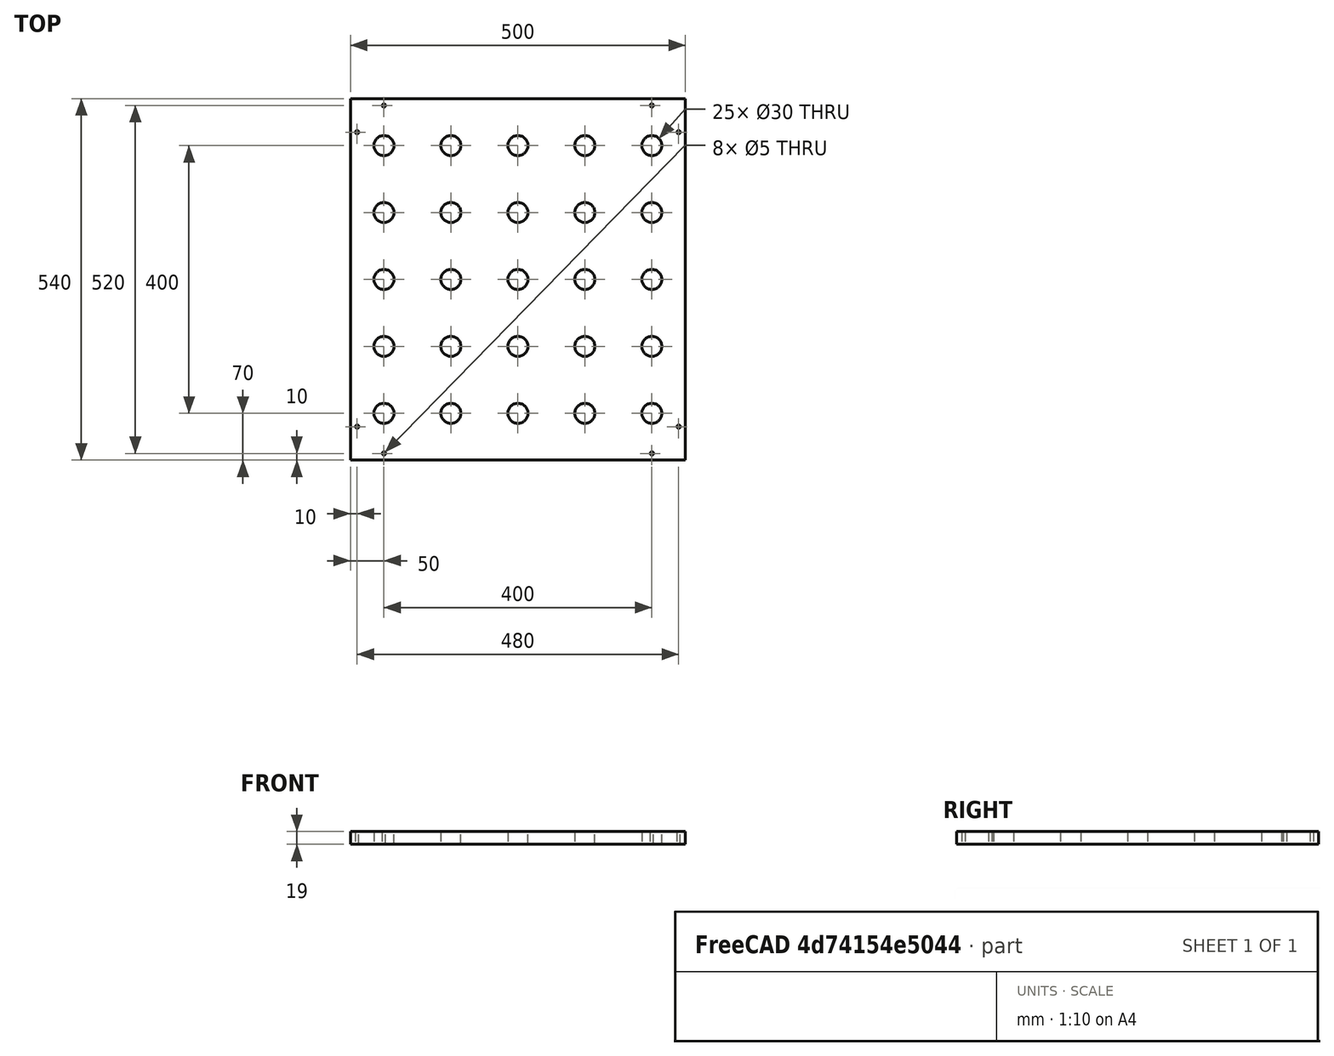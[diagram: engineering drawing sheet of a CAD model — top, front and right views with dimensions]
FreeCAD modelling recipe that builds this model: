
FCSTD DOCUMENT  (FreeCAD 0.19R)
Label: plate
License: All rights reserved
LicenseURL: http://en.wikipedia.org/wiki/All_rights_reserved
objects: TechDraw::DrawViewDimension×12, TechDraw::DrawViewPart×2, Sketcher::SketchObject×1, PartDesign::Body×1, Part::Extrusion×1, TechDraw::DrawSVGTemplate×1, TechDraw::DrawViewAnnotation×1, TechDraw::DrawPage×1
note: 3 computed .brp shape members not serialized (recipe doc carries the construction recipe); baked Part::Feature solids carry a one-line shape summary decoded from their .brp

FEATURE [Sketcher::SketchObject] Sketch
  FullyConstrained = true
  MapMode = 5
  Support = -> [XY_Plane]
  sketch-geometry (37):
    g0: LineSegment StartX=-500 StartY=540 StartZ=0 EndX=0 EndY=540 EndZ=0
    g1: LineSegment StartX=0 StartY=540 StartZ=0 EndX=0 EndY=0 EndZ=0
    g2: LineSegment StartX=0 StartY=0 StartZ=0 EndX=-500 EndY=0 EndZ=0
    g3: LineSegment StartX=-500 StartY=0 StartZ=0 EndX=-500 EndY=540 EndZ=0
    g4: Circle CenterX=-450 CenterY=470 CenterZ=0 NormalX=0 NormalY=0 NormalZ=1 AngleXU=0 Radius=15
    g5: Circle CenterX=-350 CenterY=470 CenterZ=0 NormalX=0 NormalY=0 NormalZ=1 AngleXU=0 Radius=15
    g6: Circle CenterX=-250 CenterY=470 CenterZ=0 NormalX=0 NormalY=0 NormalZ=1 AngleXU=0 Radius=15
    g7: Circle CenterX=-150 CenterY=470 CenterZ=0 NormalX=0 NormalY=0 NormalZ=1 AngleXU=0 Radius=15
    g8: Circle CenterX=-50 CenterY=470 CenterZ=0 NormalX=0 NormalY=0 NormalZ=1 AngleXU=0 Radius=15
    g9: Circle CenterX=-450 CenterY=370 CenterZ=0 NormalX=0 NormalY=0 NormalZ=1 AngleXU=0 Radius=15
    g10: Circle CenterX=-450 CenterY=270 CenterZ=0 NormalX=0 NormalY=0 NormalZ=1 AngleXU=0 Radius=15
    g11: Circle CenterX=-450 CenterY=170 CenterZ=0 NormalX=0 NormalY=0 NormalZ=1 AngleXU=0 Radius=15
    g12: Circle CenterX=-450 CenterY=70 CenterZ=0 NormalX=0 NormalY=0 NormalZ=1 AngleXU=0 Radius=15
    g13: Circle CenterX=-350 CenterY=370 CenterZ=0 NormalX=0 NormalY=0 NormalZ=1 AngleXU=0 Radius=15
    g14: Circle CenterX=-250 CenterY=370 CenterZ=0 NormalX=0 NormalY=0 NormalZ=1 AngleXU=0 Radius=15
    g15: Circle CenterX=-150 CenterY=370 CenterZ=0 NormalX=0 NormalY=0 NormalZ=1 AngleXU=0 Radius=15
    g16: Circle CenterX=-50 CenterY=370 CenterZ=0 NormalX=0 NormalY=0 NormalZ=1 AngleXU=0 Radius=15
    g17: Circle CenterX=-350 CenterY=270 CenterZ=0 NormalX=0 NormalY=0 NormalZ=1 AngleXU=0 Radius=15
    g18: Circle CenterX=-250 CenterY=270 CenterZ=0 NormalX=0 NormalY=0 NormalZ=1 AngleXU=0 Radius=15
    g19: Circle CenterX=-150 CenterY=270 CenterZ=0 NormalX=0 NormalY=0 NormalZ=1 AngleXU=0 Radius=15
    g20: Circle CenterX=-50 CenterY=270 CenterZ=0 NormalX=0 NormalY=0 NormalZ=1 AngleXU=0 Radius=15
    g21: Circle CenterX=-350 CenterY=170 CenterZ=0 NormalX=0 NormalY=0 NormalZ=1 AngleXU=0 Radius=15
    g22: Circle CenterX=-250 CenterY=170 CenterZ=0 NormalX=0 NormalY=0 NormalZ=1 AngleXU=0 Radius=15
    g23: Circle CenterX=-150 CenterY=170 CenterZ=0 NormalX=0 NormalY=0 NormalZ=1 AngleXU=0 Radius=15
    g24: Circle CenterX=-50 CenterY=170 CenterZ=0 NormalX=0 NormalY=0 NormalZ=1 AngleXU=0 Radius=15
    g25: Circle CenterX=-350 CenterY=70 CenterZ=0 NormalX=0 NormalY=0 NormalZ=1 AngleXU=0 Radius=15
    g26: Circle CenterX=-250 CenterY=70 CenterZ=0 NormalX=0 NormalY=0 NormalZ=1 AngleXU=0 Radius=15
    g27: Circle CenterX=-150 CenterY=70 CenterZ=0 NormalX=0 NormalY=0 NormalZ=1 AngleXU=0 Radius=15
    g28: Circle CenterX=-50 CenterY=70 CenterZ=0 NormalX=0 NormalY=0 NormalZ=1 AngleXU=0 Radius=15
    g29: Circle CenterX=-450 CenterY=530 CenterZ=0 NormalX=0 NormalY=0 NormalZ=1 AngleXU=0 Radius=2.5
    g30: Circle CenterX=-490 CenterY=490 CenterZ=0 NormalX=0 NormalY=0 NormalZ=1 AngleXU=0 Radius=2.5
    g31: Circle CenterX=-50 CenterY=530 CenterZ=0 NormalX=0 NormalY=0 NormalZ=1 AngleXU=0 Radius=2.5
    g32: Circle CenterX=-10 CenterY=490 CenterZ=0 NormalX=0 NormalY=0 NormalZ=1 AngleXU=0 Radius=2.5
    g33: Circle CenterX=-490 CenterY=50 CenterZ=0 NormalX=0 NormalY=0 NormalZ=1 AngleXU=0 Radius=2.5
    g34: Circle CenterX=-450 CenterY=10 CenterZ=0 NormalX=0 NormalY=0 NormalZ=1 AngleXU=0 Radius=2.5
    g35: Circle CenterX=-10 CenterY=50 CenterZ=0 NormalX=0 NormalY=0 NormalZ=1 AngleXU=0 Radius=2.5
    g36: Circle CenterX=-50 CenterY=10 CenterZ=0 NormalX=0 NormalY=0 NormalZ=1 AngleXU=0 Radius=2.5
  constraints (110):
    c: Coincident(g0,g1)
    c: Coincident(g1,g2)
    c: Coincident(g2,g3)
    c: Coincident(g3,g0)
    c: Horizontal(g0)
    c: Horizontal(g2)
    c: Vertical(g1)
    c: Vertical(g3)
    c: Distance(g0) = 500
    c: Distance(g3) = 540
    c: Diameter(g4) = 30
    c: DistanceX(g0,g4) = 50
    c: DistanceY(g4,g0) = 70
    c: DistanceX(g4,g5) = 100
    c: DistanceX(g5,g6) = 100
    c: DistanceX(g6,g7) = 100
    c: DistanceX(g7,g8) = 100
    c: DistanceY(g9,g4) = 100
    c: DistanceY(g10,g9) = 100
    c: DistanceY(g11,g10) = 100
    c: DistanceY(g12,g11) = 100
    c: Equal(g4,g5)
    c: Equal(g5,g6)
    c: Equal(g6,g7)
    c: Equal(g7,g8)
    c: Equal(g4,g9)
    c: Equal(g9,g10)
    c: Equal(g10,g11)
    c: Equal(g11,g12)
    c: Horizontal(g4,g5)
    c: Horizontal(g5,g6)
    c: Horizontal(g6,g7)
    c: Horizontal(g7,g8)
    c: Vertical(g4,g9)
    c: Vertical(g9,g10)
    c: Vertical(g10,g11)
    c: Vertical(g11,g12)
    c: Equal(g9,g13)
    c: Equal(g13,g14)
    c: Equal(g14,g15)
    c: Equal(g15,g16)
    c: Equal(g10,g17)
    c: Equal(g17,g18)
    c: Equal(g18,g19)
    c: Equal(g19,g20)
    c: Equal(g11,g21)
    c: Equal(g21,g22)
    c: Equal(g22,g23)
    c: Equal(g23,g24)
    c: Equal(g12,g25)
    c: Equal(g25,g26)
    c: Equal(g26,g27)
    c: Equal(g27,g28)
    c: Horizontal(g12,g25)
    c: Horizontal(g25,g26)
    c: Horizontal(g26,g27)
    c: Horizontal(g27,g28)
    c: Horizontal(g11,g21)
    c: Horizontal(g21,g22)
    c: Horizontal(g22,g23)
    c: Horizontal(g23,g24)
    c: Horizontal(g10,g17)
    c: Horizontal(g17,g18)
    c: Horizontal(g18,g19)
    c: Horizontal(g19,g20)
    c: Horizontal(g9,g13)
    c: Horizontal(g13,g14)
    c: Horizontal(g14,g15)
    c: Horizontal(g15,g16)
    c: Vertical(g5,g13)
    c: Vertical(g6,g14)
    c: Vertical(g7,g15)
    c: Vertical(g8,g16)
    c: Vertical(g13,g17)
    c: Vertical(g14,g18)
    c: Vertical(g15,g19)
    c: Vertical(g16,g20)
    c: Vertical(g17,g21)
    c: Vertical(g18,g22)
    c: Vertical(g19,g23)
    c: Vertical(g20,g24)
    c: Vertical(g21,g25)
    c: Vertical(g26,g22)
    c: Vertical(g23,g27)
    c: Vertical(g24,g28)
    c: Diameter(g29) = 5
    c: Distance(g29,g3) = 50
    c: Distance(g29,g0) = 10
    c: Equal(g29,g30) = 5
    c: Distance(g30,g3) = 10
    c: Distance(g30,g0) = 50
    c: Equal(g29,g31) = 5
    c: Distance(g35,g2) = 50
    c: Distance(g36,g1) = 50
    c: Distance(g36,g2) = 10
    c: Distance(g35,g1) = 10
    c: Distance(g33,g2) = 50
    c: Distance(g34,g3) = 50
    c: Distance(g34,g2) = 10
    c: Distance(g33,g3) = 10
    c: Distance(g32,g1) = 10
    c: Distance(g31,g0) = 10
    c: Distance(g31,g1) = 50
    c: Distance(g32,g0) = 50
    c: Equal(g31,g32)
    c: Equal(g30,g33)
    c: Equal(g33,g34)
    c: Equal(g32,g35)
    c: Equal(g35,g36)
    c: Coincident(g1,g-1)
FEATURE [PartDesign::Body] Body
  Group = -> [Sketch]
  Origin = -> Origin
FEATURE [Part::Extrusion] Extrude
  Base = -> Sketch
  Dir = (0,0,1)
  DirMode = 2
  FaceMakerClass = Part::FaceMakerBullseye
  LengthFwd = 19
  LengthRev = 0
  Solid = true
  Symmetric = false
FEATURE [TechDraw::DrawSVGTemplate] Template
  EditableTexts = Designed_by_Name=Erich Studer; Drawing_number=<tag, commit>; FC-Date=xx.xx.xxxx; FC-SC=n/a; FC-SH=1/1; FC-Title=Light_Installation - Plate; Subtitle=github.com/<owner>/Light_Installation; Weight=n/a
  Height = 210
  Orientation = 1
  Width = 297
FEATURE [TechDraw::DrawViewPart] View
  CoarseView = false
  Direction = (0,0,1)
  Focus = 100
  HardHidden = false
  IsoCount = 0
  IsoHidden = false
  IsoVisible = false
  LockPosition = false
  Perspective = false
  Rotation = 0
  Scale = 0.25
  ScaleType = 0
  SeamHidden = false
  SeamVisible = true
  SmoothHidden = false
  SmoothVisible = true
  Source = -> [Sketch]
  X = 95.3571
  XDirection = (0,1,0)
  Y = 125.229
FEATURE [TechDraw::DrawViewDimension] Dimension001
  Arbitrary = false
  ArbitraryTolerances = false
  EqualTolerance = true
  FormatSpec = %.0f
  FormatSpecOverTolerance = %+.2f
  FormatSpecUnderTolerance = %+.2f
  Inverted = false
  LockPosition = false
  MeasureType = 1
  OverTolerance = 0
  References2D = -> [View]
  Rotation = 0
  Scale = 0.25
  ScaleType = 0
  TheoreticalExact = false
  Type = 2
  UnderTolerance = 0
  X = -78.7322
  Y = 1.37143
FEATURE [TechDraw::DrawViewDimension] Dimension
  Arbitrary = false
  ArbitraryTolerances = false
  EqualTolerance = true
  FormatSpec = %.0f
  FormatSpecOverTolerance = %+.2f
  FormatSpecUnderTolerance = %+.2f
  Inverted = false
  LockPosition = false
  MeasureType = 1
  OverTolerance = 0
  References2D = -> [View]
  Rotation = 0
  Scale = 0.25
  ScaleType = 0
  TheoreticalExact = false
  Type = 1
  UnderTolerance = 0
  X = -1.02857
  Y = 74.5
FEATURE [TechDraw::DrawViewDimension] Dimension002
  Arbitrary = false
  ArbitraryTolerances = false
  EqualTolerance = true
  FormatSpec = ⌀%.0f
  FormatSpecOverTolerance = %+.2f
  FormatSpecUnderTolerance = %+.2f
  Inverted = false
  LockPosition = false
  MeasureType = 1
  OverTolerance = 0
  References2D = -> [View]
  Rotation = 0
  Scale = 0.25
  ScaleType = 0
  TheoreticalExact = false
  Type = 5
  UnderTolerance = 0
  X = -45.1389
  Y = 60.8466
FEATURE [TechDraw::DrawViewDimension] Dimension004
  Arbitrary = false
  ArbitraryTolerances = false
  EqualTolerance = true
  FormatSpec = %.0f
  FormatSpecOverTolerance = %+.2f
  FormatSpecUnderTolerance = %+.2f
  Inverted = false
  LockPosition = false
  MeasureType = 1
  OverTolerance = 0
  References2D = -> [View]
  Rotation = 0
  Scale = 0.25
  ScaleType = 0
  TheoreticalExact = false
  Type = 1
  UnderTolerance = 0
  X = -58.4179
  Y = 38.4938
FEATURE [TechDraw::DrawViewDimension] Dimension005
  Arbitrary = false
  ArbitraryTolerances = false
  EqualTolerance = true
  FormatSpec = ⌀%.0f
  FormatSpecOverTolerance = %+.2f
  FormatSpecUnderTolerance = %+.2f
  Inverted = false
  LockPosition = false
  MeasureType = 1
  OverTolerance = 0
  References2D = -> [View]
  Rotation = 0
  Scale = 0.25
  ScaleType = 0
  TheoreticalExact = false
  Type = 5
  UnderTolerance = 0
  X = -14.641
  Y = 59.4694
FEATURE [TechDraw::DrawViewDimension] Dimension006
  Arbitrary = false
  ArbitraryTolerances = false
  EqualTolerance = true
  FormatSpec = %.0f
  FormatSpecOverTolerance = %+.2f
  FormatSpecUnderTolerance = %+.2f
  Inverted = false
  LockPosition = false
  MeasureType = 1
  OverTolerance = 0
  References2D = -> [View]
  Rotation = 0
  Scale = 0.25
  ScaleType = 0
  TheoreticalExact = false
  Type = 1
  UnderTolerance = 0
  X = -61.8201
  Y = -41.7494
FEATURE [TechDraw::DrawViewDimension] Dimension007
  Arbitrary = false
  ArbitraryTolerances = false
  EqualTolerance = true
  FormatSpec = %.0f
  FormatSpecOverTolerance = %+.2f
  FormatSpecUnderTolerance = %+.2f
  Inverted = false
  LockPosition = false
  MeasureType = 1
  OverTolerance = 0
  References2D = -> [View]
  Rotation = 0
  Scale = 0.25
  ScaleType = 0
  TheoreticalExact = false
  Type = 2
  UnderTolerance = 0
  X = -61.7875
  Y = -54.0511
FEATURE [TechDraw::DrawViewDimension] Dimension008
  Arbitrary = false
  ArbitraryTolerances = false
  EqualTolerance = true
  FormatSpec = %.0f
  FormatSpecOverTolerance = %+.2f
  FormatSpecUnderTolerance = %+.2f
  Inverted = false
  LockPosition = false
  MeasureType = 1
  OverTolerance = 0
  References2D = -> [View]
  Rotation = 0
  Scale = 0.25
  ScaleType = 0
  TheoreticalExact = false
  Type = 1
  UnderTolerance = 0
  X = 59.0399
  Y = -51.1152
FEATURE [TechDraw::DrawViewDimension] Dimension009
  Arbitrary = false
  ArbitraryTolerances = false
  EqualTolerance = true
  FormatSpec = %.0f
  FormatSpecOverTolerance = %+.2f
  FormatSpecUnderTolerance = %+.2f
  Inverted = false
  LockPosition = false
  MeasureType = 1
  OverTolerance = 0
  References2D = -> [View]
  Rotation = 0
  Scale = 0.25
  ScaleType = 0
  TheoreticalExact = false
  Type = 2
  UnderTolerance = 0
  X = 41.5111
  Y = -54.5388
FEATURE [TechDraw::DrawViewDimension] Dimension010
  Arbitrary = false
  ArbitraryTolerances = false
  EqualTolerance = true
  FormatSpec = %.0f
  FormatSpecOverTolerance = %+.2f
  FormatSpecUnderTolerance = %+.2f
  Inverted = false
  LockPosition = false
  MeasureType = 1
  OverTolerance = 0
  References2D = -> [View]
  Rotation = 0
  Scale = 0.25
  ScaleType = 0
  TheoreticalExact = false
  Type = 1
  UnderTolerance = 0
  X = -11.6962
  Y = -4.47806
FEATURE [TechDraw::DrawViewDimension] Dimension011
  Arbitrary = false
  ArbitraryTolerances = false
  EqualTolerance = true
  FormatSpec = %.0f
  FormatSpecOverTolerance = %+.2f
  FormatSpecUnderTolerance = %+.2f
  Inverted = false
  LockPosition = false
  MeasureType = 1
  OverTolerance = 0
  References2D = -> [View]
  Rotation = 0
  Scale = 0.25
  ScaleType = 0
  TheoreticalExact = false
  Type = 2
  UnderTolerance = 0
  X = 6.72204
  Y = 15.4755
FEATURE [TechDraw::DrawViewDimension] Dimension012
  Arbitrary = false
  ArbitraryTolerances = false
  EqualTolerance = true
  FormatSpec = %.0f
  FormatSpecOverTolerance = %+.2f
  FormatSpecUnderTolerance = %+.2f
  Inverted = false
  LockPosition = false
  MeasureType = 1
  OverTolerance = 0
  References2D = -> [View]
  Rotation = 0
  Scale = 0.25
  ScaleType = 0
  TheoreticalExact = false
  Type = 2
  UnderTolerance = 0
  X = 8.72648
  Y = 58.4316
FEATURE [TechDraw::DrawViewPart] View001
  CoarseView = false
  Direction = (0.734,-0.237,0.637)
  Focus = 100
  HardHidden = false
  IsoCount = 0
  IsoHidden = false
  IsoVisible = false
  LockPosition = false
  Perspective = false
  Rotation = 0
  Scale = 0.1
  ScaleType = 0
  SeamHidden = false
  SeamVisible = true
  SmoothHidden = false
  SmoothVisible = true
  Source = -> [Extrude]
  X = 233.569
  XDirection = (0.241,0.967,0.082)
  Y = 117.519
FEATURE [TechDraw::DrawViewAnnotation] Annotation
  Font = osifont
  LineSpace = 80
  LockPosition = false
  MaxWidth = -1
  Rotation = 0
  Scale = 0.25
  ScaleType = 0
  Text = color: black
  TextSize = 5
  TextStyle = 0
  X = 213.288
  Y = 141.619
FEATURE [TechDraw::DrawPage] Page  label="TechDraw"
  KeepUpdated = true
  NextBalloonIndex = 1
  ProjectionType = 0
  Scale = 0.25
  Template = -> Template
  Views = -> [View,Dimension,Dimension001,Dimension002,Dimension004,Dimension005,Dimension006,Dimension007,Dimension008,Dimension009,Dimension010,Dimension011,Dimension012,View001,Annotation]
